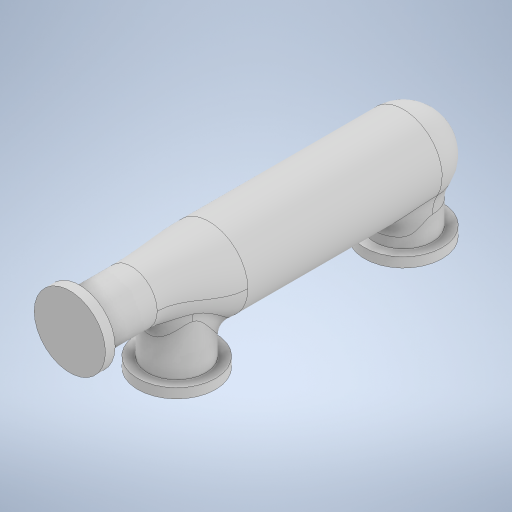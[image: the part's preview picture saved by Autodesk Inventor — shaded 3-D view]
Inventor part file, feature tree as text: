
AUTODESK INVENTOR PART (.ipt)
format: ipt  version: 2023 (Build 270158000, 158)  size: 444,416 bytes
history: native  units: in
note: dims shown in document units (in); Inventor stores cm internally (conversion verified against a paired STEP export)
features: sketch x6, extrude x5, other x2, fillet x2, revolve x1, plane x1, loft x1, projected_geometry x1
ambient origin geometry x8: Origin, YZ Plane, XZ Plane, XY Plane, X Axis, Y Axis, Z Axis, Center Point
bodies: Solid1 (feature_tree)
feature tree (19):
  other  "intake_manifold_r"
  revolve  "Revolution1"  [1 undecoded]
  plane  "Work Plane1"
  loft  "Loft1"
  extrude  "Extrusion1"  Depth=0.3937in
  fillet  "Fillet1"  Radius=0.3937in
  extrude  "Extrusion2"  Depth=0.3937in
  extrude  "Extrusion3"  Depth=11.0in TaperAngle=0.0deg
  extrude  "Extrusion5"  Depth=1.5in
  fillet  "Fillet3"  Radius=1.5in
  extrude  "Extrusion6"  Depth=1.5in
  sketch  "Sketch3"  dims[d3=30.0in d4=6.0in]
  other  "Edges1"
  sketch  "Sketch4"  dims[d5=90.0deg d6=12.0in]
  sketch  "Sketch5"  dims[d7=8.0in d8=2.0in d9=0.3937in d10=90.0deg]
  projected_geometry  "Projected Loop1"
  sketch  "Sketch6"  dims[d13=0.3937in d14=90.0deg d15=9.0in]
  sketch  "Sketch8"  dims[d16=9.0in d17=11.0in d18=0.0in]
  sketch  "Sketch9"  dims[d20=12.0in d21=12.0in d22=1.5in d23=0.0in d24=6.0in d25=6.0in d26=6.0in d27=0.0in d28=2.0in d29=0.1969in d30=6.0in d31=0.3937in d33=1.0in d34=0.0in d48=2.5in d49=5.0in d50=8.0in d51=0.0in d52=3.0in d53=3.0in d54=3.0in d55=0.0in d56=3.0in d57=0.1969in d58=2.0in d59=0.2953in d60=2.0in d61=0.0984in d62=11.0in d63=1.5in d64=0.0in d65=0.5in d66=0.0344in d67=0.5in d68=0.0344in]
note: 1 required parameter value undecoded (feature->parameter linkage not recoverable at this tier; creation-order binding heuristic only, values carry confidence <= 0.55)
